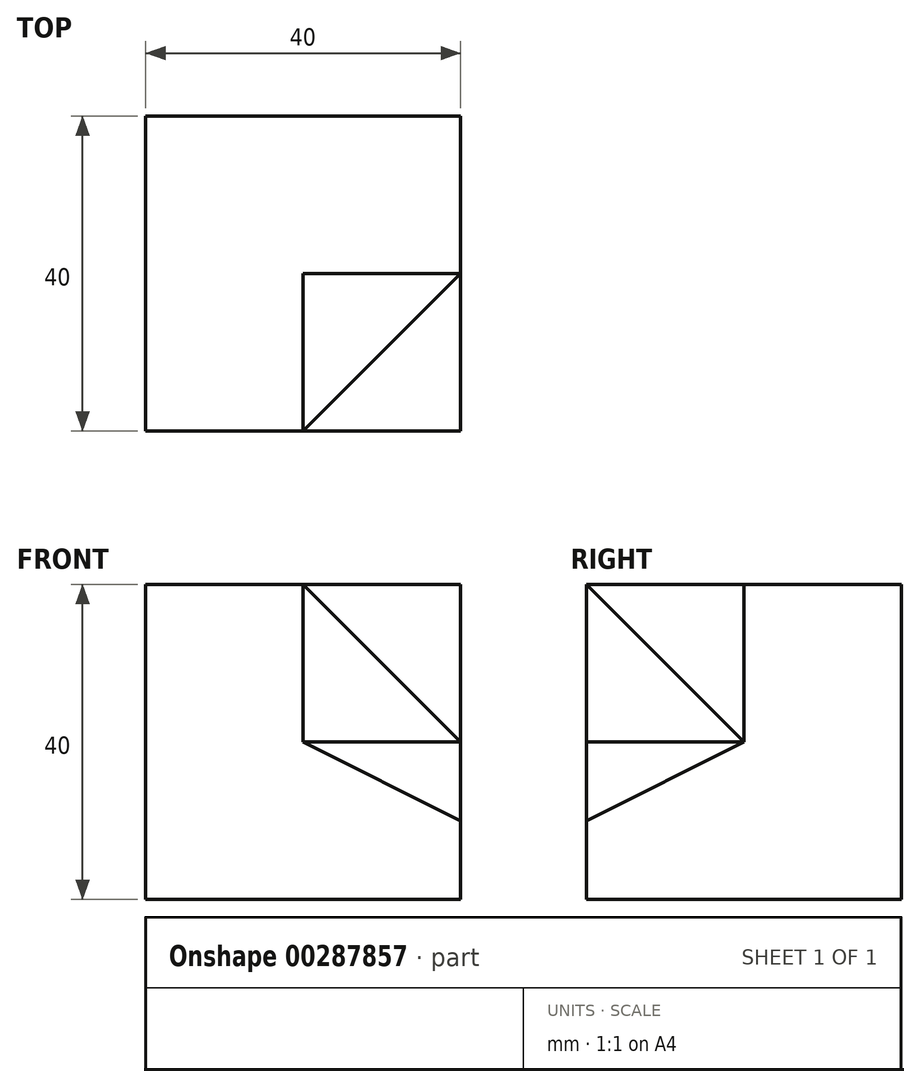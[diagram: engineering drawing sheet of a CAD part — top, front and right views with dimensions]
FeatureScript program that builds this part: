
annotation { "Feature Type Name" : "Feature", "Feature Type Description" : "" }
export const myFeature = defineFeature(function(context is Context, id is Id, definition is map)
    precondition{}
    {
        {
            var Q0;
            Q0=qCreatedBy(makeId("Front.planeOp"),FACE);
            var sketch = newSketch(context, id + "F0", { "sketchPlane" : qUnion([Q0])});
            skLineSegment(sketch, "E0.bottom", {"start": v(0, 0) * mm, "end": v(40, 0) * mm});
            skLineSegment(sketch, "E0.top", {"start": v(0, 40) * mm, "end": v(40, 40) * mm});
            skLineSegment(sketch, "E0.left", {"start": v(0, 0) * mm, "end": v(0, 40) * mm});
            skLineSegment(sketch, "E0.right", {"start": v(40, 0) * mm, "end": v(40, 40) * mm});
            skSolve(sketch);
        }
        {
            var Q0;
            Q0=qSketchRegion(id+"F0",true);
            extrude(context, id + "F1", {"entities" : qUnion([Q0]), "depth" : 40 * mm});
        }
        {
            var Q0;
            Q0=makeQuery(id+"F1.opExtrude","CAP_FACE",FACE,{"disambiguationData":[OSD([sQuery(id+"F0.wireOp",EDGE,"E0.bottom"),sQuery(id+"F0.wireOp",EDGE,"E0.top"),sQuery(id+"F0.wireOp",EDGE,"E0.left"),sQuery(id+"F0.wireOp",EDGE,"E0.right")])],"isStart":false});
            var sketch = newSketch(context, id + "F2", { "sketchPlane" : qUnion([Q0])});
            skPoint(sketch, "E1.oppositeSnap0", {"position": v(20, 0) * mm});
            skPoint(sketch, "E1.oppositeSnap1", {"position": v(0, 20) * mm});
            skLineSegment(sketch, "E1.bottom", {"start": v(40, 40) * mm, "end": v(20, 40) * mm});
            skLineSegment(sketch, "E1.top", {"start": v(40, 20) * mm, "end": v(20, 20) * mm});
            skLineSegment(sketch, "E1.left", {"start": v(40, 40) * mm, "end": v(40, 20) * mm});
            skLineSegment(sketch, "E1.right", {"start": v(20, 40) * mm, "end": v(20, 20) * mm});
            skSolve(sketch);
        }
        {
            var Q0;
            Q0=qSketchRegion(id+"F2",true);
            extrude(context, id + "F3", {"entities" : qUnion([Q0]), "operationType" : NewBodyOperationType.REMOVE, "oppositeDirection" : true, "depth" : 20 * mm});
        }
        {
            var Q0;
            Q0=makeQuery(id+"F1.opExtrude","CAP_EDGE",EDGE,{"disambiguationData":[OSD([sQuery(id+"F0.wireOp",EDGE,"E0.right")])],"isStart":false});
            cPoint(context, id + "F4", {"entities" : qUnion([Q0]), "parameter" : 0.5});
        }
        {
            var Q0;
            Q0=makeQuery(id+"F3.boolean.opBoolean","COPY",VERTEX,{"derivedFrom":makeQuery(id+"F3.opExtrude","CAP_VERTEX",VERTEX,{"disambiguationData":[OSD([sQuery(id+"F0.wireOp",EDGE,"E0.right"),sQuery(id+"F2.wireOp",EDGE,"E1.top"),sQuery(id+"F2.wireOp",EDGE,"E1.left")])],"isStart":false})});
            var Q1;
            Q1=makeQuery(id+"F3.boolean.opBoolean","COPY",VERTEX,{"derivedFrom":makeQuery(id+"F3.opExtrude","CAP_VERTEX",VERTEX,{"disambiguationData":[OSD([sQuery(id+"F2.wireOp",EDGE,"E1.top"),sQuery(id+"F2.wireOp",EDGE,"E1.right")])],"isStart":true})});
            var Q2;
            Q2=qCreatedBy(id+"F4",VERTEX);
            cPlane(context, id + "F5", {"entities" : qUnion([Q0, Q1, Q2]), "cplaneType" : CPlaneType.THREE_POINT, "offset" : 25 * mm, "width" : 150 * mm, "height" : 150 * mm});
        }
        {
            var Q0;
            Q0=qCreatedBy(id+"F5.planeOp",FACE);
            var sketch = newSketch(context, id + "F6", { "sketchPlane" : qUnion([Q0])});
            skPoint(sketch, "E2.0", {"position": v(25.56, 8.94) * mm});
            skPoint(sketch, "E3.0", {"position": v(3.65, 26.83) * mm});
            skPoint(sketch, "E4.0", {"position": v(25.56, 31.3) * mm});
            skLineSegment(sketch, "E5", {"start": v(25.56, 8.94) * mm, "end": v(3.65, 26.83) * mm});
            skLineSegment(sketch, "E6", {"start": v(25.56, 31.3) * mm, "end": v(3.65, 26.83) * mm});
            skLineSegment(sketch, "E7", {"start": v(25.56, 8.94) * mm, "end": v(25.56, 31.3) * mm});
            skSolve(sketch);
        }
        {
            var Q0;
            Q0=qSketchRegion(id+"F6",true);
            extrude(context, id + "F7", {"entities" : qUnion([Q0]), "operationType" : NewBodyOperationType.REMOVE, "endBound" : BoundingType.THROUGH_ALL, "oppositeDirection" : true, "depth" : 25 * mm});
        }
        {
            var Q0;
            Q0=makeQuery(id+"F3.boolean.opBoolean","COPY",FACE,{"derivedFrom":makeQuery(id+"F3.opExtrude","CAP_FACE",FACE,{"disambiguationData":[OSD([sQuery(id+"F2.wireOp",EDGE,"E1.bottom"),sQuery(id+"F2.wireOp",EDGE,"E1.top"),sQuery(id+"F2.wireOp",EDGE,"E1.left"),sQuery(id+"F2.wireOp",EDGE,"E1.right")])],"isStart":false})});
            var sketch = newSketch(context, id + "F8", { "sketchPlane" : qUnion([Q0])});
            skLineSegment(sketch, "E8", {"start": v(20, 40) * mm, "end": v(40, 20) * mm});
            skLineSegment(sketch, "E9.0", {"start": v(20, 40) * mm, "end": v(20, 20) * mm});
            skLineSegment(sketch, "E10.0", {"start": v(40, 20) * mm, "end": v(20, 20) * mm});
            skSolve(sketch);
        }
        {
            var Q0;
            Q0 = qSketchRegion(id + "F8", true);
            var Q1;
            Q1=makeQuery(id+"F1.opExtrude","CAP_FACE",FACE,{"disambiguationData":[OSD([sQuery(id+"F0.wireOp",EDGE,"E0.bottom"),sQuery(id+"F0.wireOp",EDGE,"E0.top"),sQuery(id+"F0.wireOp",EDGE,"E0.left"),sQuery(id+"F0.wireOp",EDGE,"E0.right")])],"isStart":false});
            extrude(context, id + "F9", {"entities" : qUnion([Q0]), "operationType" : NewBodyOperationType.ADD, "endBound" : BoundingType.UP_TO_SURFACE, "endBoundEntityFace" : qUnion([Q1]), "depth" : 25 * mm});
        }
        {
            var Q0;
            Q0=makeQuery(id+"F9.opExtrude","SWEPT_FACE",FACE,{"disambiguationData":[OSD([sQuery(id+"F8.wireOp",EDGE,"E10.0")])]});
            var sketch = newSketch(context, id + "F10", { "sketchPlane" : qUnion([Q0])});
            skLineSegment(sketch, "E11.0", {"start": v(40, 20) * mm, "end": v(20, 40) * mm});
            skLineSegment(sketch, "E12.0", {"start": v(40, 40) * mm, "end": v(20, 40) * mm});
            skLineSegment(sketch, "E13.0", {"start": v(40, 20) * mm, "end": v(40, 40) * mm});
            skSolve(sketch);
        }
        {
            var Q0;
            Q0 = qSketchRegion(id + "F10", true);
            var Q1;
            Q1=makeQuery(id+"F1.opExtrude","SWEPT_FACE",FACE,{"disambiguationData":[OSD([sQuery(id+"F0.wireOp",EDGE,"E0.top")])]});
            extrude(context, id + "F11", {"entities" : qUnion([Q0]), "operationType" : NewBodyOperationType.REMOVE, "endBound" : BoundingType.UP_TO_SURFACE, "oppositeDirection" : true, "endBoundEntityFace" : qUnion([Q1]), "depth" : 25 * mm});
        }
    });
